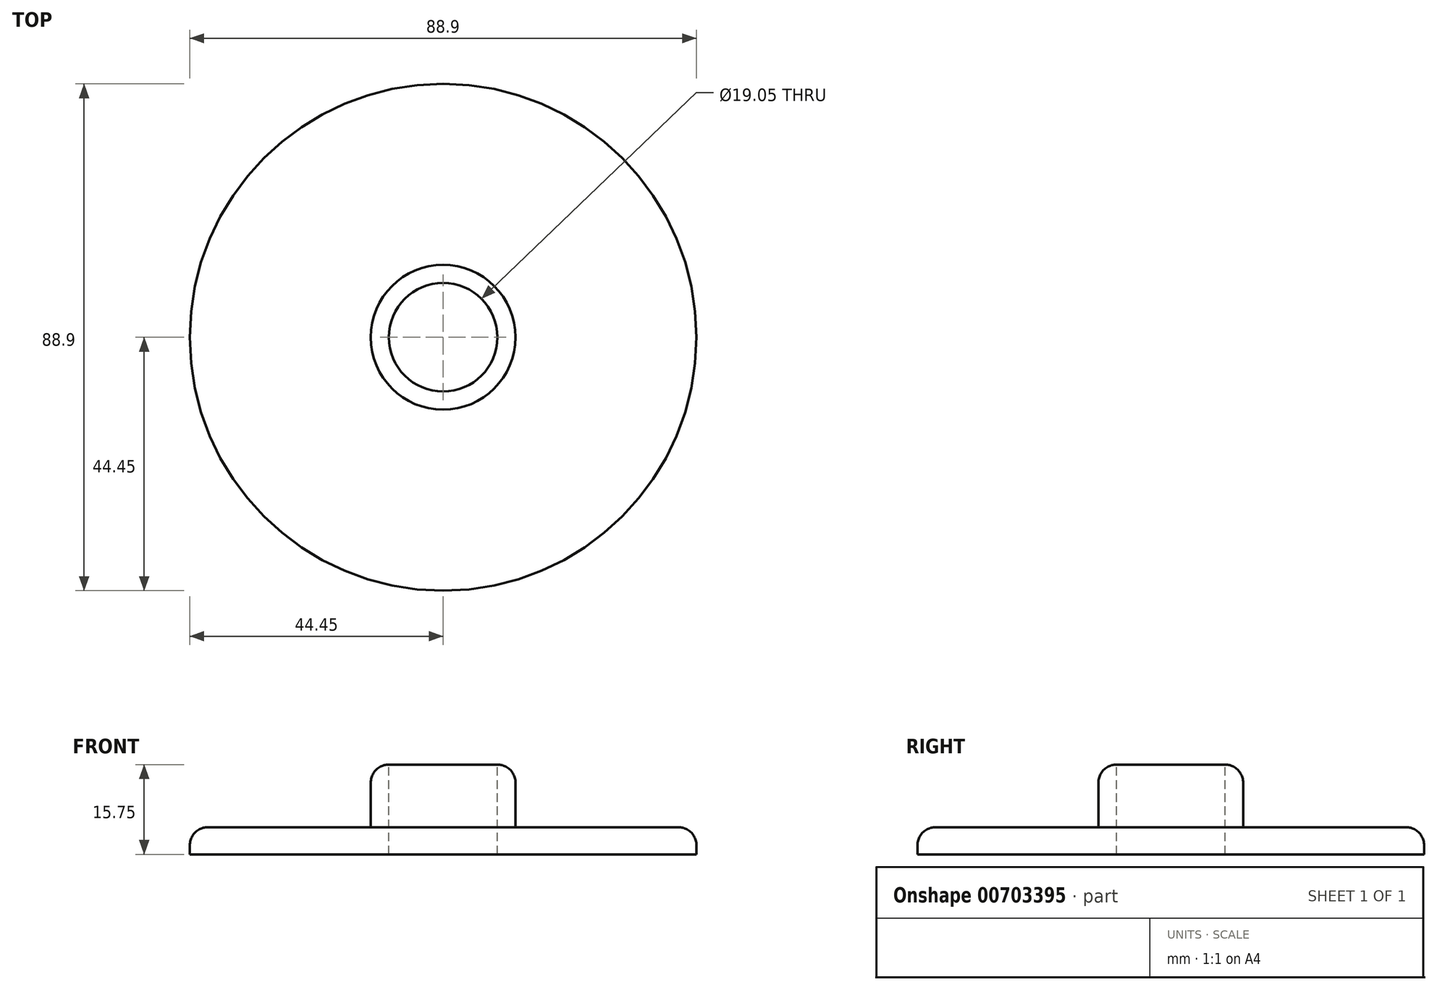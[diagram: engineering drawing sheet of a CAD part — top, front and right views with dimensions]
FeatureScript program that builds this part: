
annotation { "Feature Type Name" : "Feature", "Feature Type Description" : "" }
export const myFeature = defineFeature(function(context is Context, id is Id, definition is map)
    precondition{}
    {
        {
            var Q0;
            Q0=qCreatedBy(makeId("Top.planeOp"),FACE);
            var sketch = newSketch(context, id + "F0", { "sketchPlane" : qUnion([Q0])});
            skCircle(sketch, "E0", {"center": v(0, 0) * mm, "radius": 44.45 * mm});
            skSolve(sketch);
        }
        {
            var Q0;
            Q0 = qSketchRegion(id + "F0", true);
            extrude(context, id + "F1", {"entities" : qUnion([Q0]), "depth" : 4.76 * mm, "offsetDistance" : 25.4 * mm});
        }
        {
            var Q0;
            Q0=makeQuery(id+"F1.opExtrude","CAP_FACE",FACE,{"disambiguationData":[OSD([sQuery(id+"F0.wireOp",EDGE,"E0")])],"isStart":false});
            var sketch = newSketch(context, id + "F2", { "sketchPlane" : qUnion([Q0])});
            skCircle(sketch, "E1", {"center": v(0, 0) * mm, "radius": 9.52 * mm});
            skSolve(sketch);
        }
        {
            var Q0;
            Q0=sQuery(id+"F2.wireOp",VERTEX,"E1.center");
            var Q1;
            Q1=makeQuery(id+"F1.opExtrude","SWEPT_BODY",BODY,{"disambiguationData":[OSD([sQuery(id+"F0.wireOp",EDGE,"E0")])]});
            hole(context, id + "F3", {"style" : HoleStyle.SIMPLE, "endStyle" : HoleEndStyle.THROUGH, "holeDiameter" : 19.05 * mm, "majorDiameter" : 6.35 * mm, "isTappedThrough" : true, "tappedDepth" : 12.7 * mm, "tapClearance" : 3, "locations" : qUnion([Q0]), "scope" : qUnion([Q1])});
        }
        {
            var Q0;
            Q0=makeQuery(id+"F1.opExtrude","CAP_FACE",FACE,{"disambiguationData":[OSD([sQuery(id+"F0.wireOp",EDGE,"E0")])],"isStart":false});
            var sketch = newSketch(context, id + "F4", { "sketchPlane" : qUnion([Q0])});
            skCircle(sketch, "E2", {"center": v(0, 0) * mm, "radius": 12.7 * mm});
            skCircle(sketch, "E3", {"center": v(0, 0) * mm, "radius": 9.53 * mm});
            skSolve(sketch);
        }
        {
            var Q0;
            Q0 = qSketchRegion(id + "F4", true);
            extrude(context, id + "F5", {"entities" : qUnion([Q0]), "operationType" : NewBodyOperationType.ADD, "depth" : 11 * mm, "offsetDistance" : 25.4 * mm});
        }
        {
            var Q0;
            Q0=makeQuery(id+"F5.opExtrude","CAP_EDGE",EDGE,{"disambiguationData":[OSD([sQuery(id+"F4.wireOp",EDGE,"E2")])],"isStart":false});
            var Q1;
            Q1=makeQuery(id+"F5.opExtrude","CAP_EDGE",EDGE,{"disambiguationData":[OSD([sQuery(id+"F4.wireOp",EDGE,"E2")])],"isStart":true});
            var Q2;
            Q2=makeQuery(id+"F1.opExtrude","CAP_EDGE",EDGE,{"disambiguationData":[OSD([sQuery(id+"F0.wireOp",EDGE,"E0")])],"isStart":false});
            fillet(context, id + "F6", {"entities" : qUnion([Q0, Q1, Q2]), "radius" : 3.17 * mm, "tangentPropagation" : true, "allowEdgeOverflow" : false});
        }
    });
